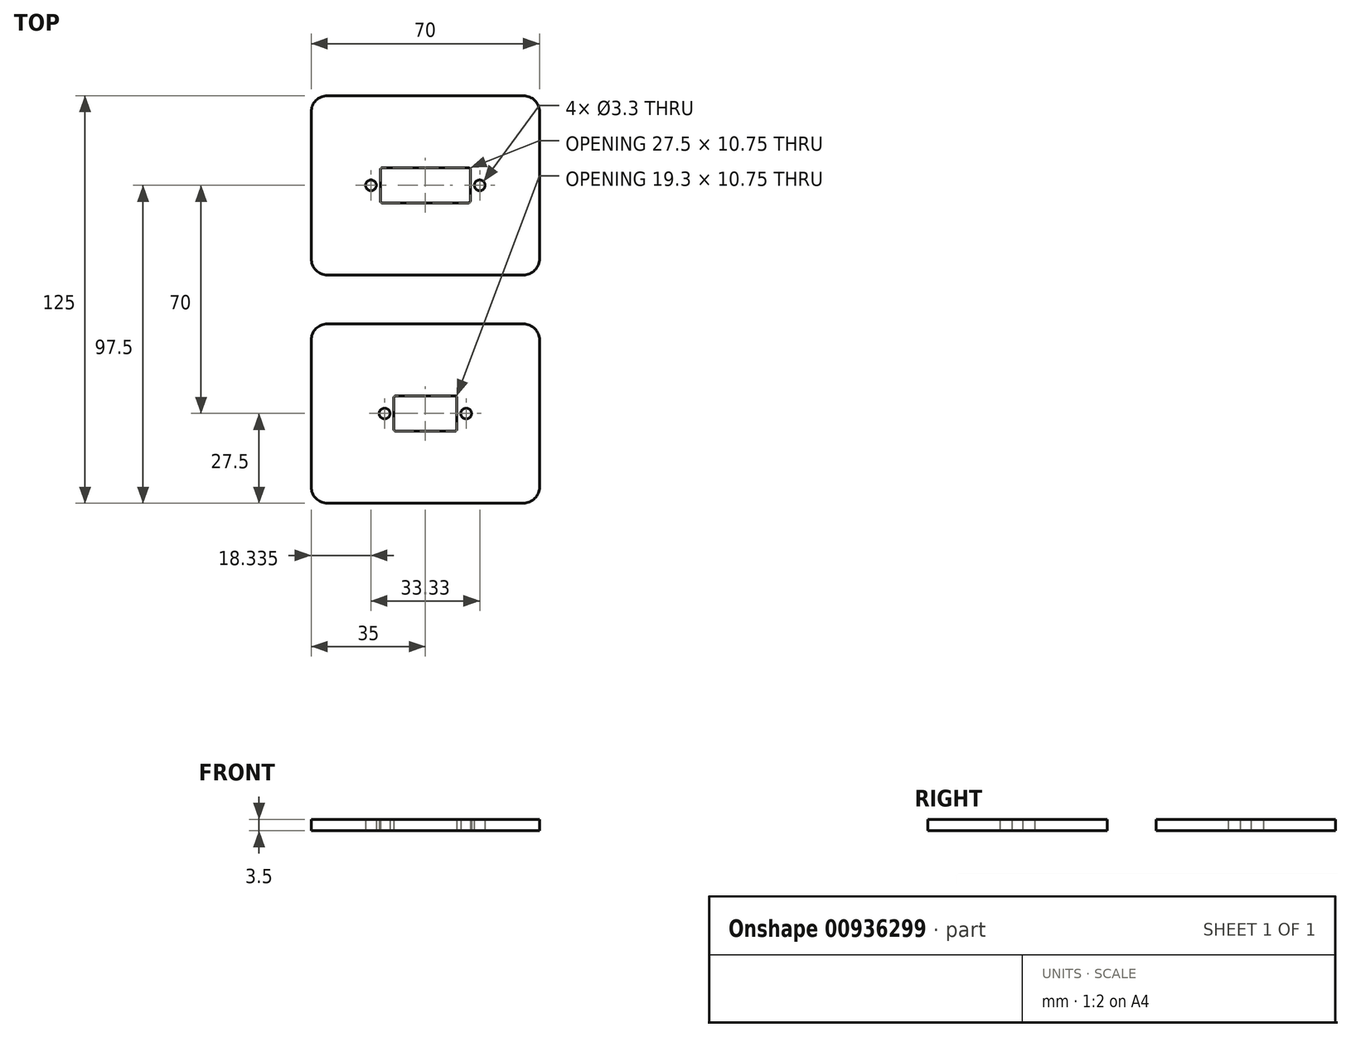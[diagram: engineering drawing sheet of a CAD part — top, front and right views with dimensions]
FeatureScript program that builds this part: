
annotation { "Feature Type Name" : "Feature", "Feature Type Description" : "" }
export const myFeature = defineFeature(function(context is Context, id is Id, definition is map)
    precondition{}
    {
        {
            var Q0;
            Q0=qCreatedBy(makeId("Top.planeOp"),FACE);
            var sketch = newSketch(context, id + "F0", { "sketchPlane" : qUnion([Q0])});
            skPoint(sketch, "E0.middle", {"position": v(0, 0) * mm});
            skLineSegment(sketch, "E1.bottom", {"start": v(35, -27.5) * mm, "end": v(-35, -27.5) * mm});
            skLineSegment(sketch, "E1.top", {"start": v(35, 27.5) * mm, "end": v(-35, 27.5) * mm});
            skLineSegment(sketch, "E1.left", {"start": v(35, -27.5) * mm, "end": v(35, 27.5) * mm});
            skLineSegment(sketch, "E1.right", {"start": v(-35, -27.5) * mm, "end": v(-35, 27.5) * mm});
            skLineSegment(sketch, "E2.bottom", {"start": v(13.75, -5.37) * mm, "end": v(-13.75, -5.38) * mm});
            skLineSegment(sketch, "E2.top", {"start": v(13.75, 5.38) * mm, "end": v(-13.75, 5.37) * mm});
            skLineSegment(sketch, "E2.left", {"start": v(13.75, -5.37) * mm, "end": v(13.75, 5.38) * mm});
            skLineSegment(sketch, "E2.right", {"start": v(-13.75, -5.38) * mm, "end": v(-13.75, 5.37) * mm});
            skCircle(sketch, "E3", {"center": v(0, 0) * mm, "radius": 16.66 * mm, "construction": true});
            skCircle(sketch, "E4", {"center": v(16.66, 0) * mm, "radius": 1.65 * mm});
            skPoint(sketch, "E4.centerSnap0", {"position": v(13.75, 0) * mm});
            skCircle(sketch, "E5", {"center": v(-16.66, 0) * mm, "radius": 1.65 * mm});
            skPoint(sketch, "E6.middle", {"position": v(0, -70) * mm});
            skLineSegment(sketch, "E7.bottom", {"start": v(35, -97.5) * mm, "end": v(-35, -97.5) * mm});
            skLineSegment(sketch, "E7.top", {"start": v(35, -42.5) * mm, "end": v(-35, -42.5) * mm});
            skLineSegment(sketch, "E7.left", {"start": v(35, -97.5) * mm, "end": v(35, -42.5) * mm});
            skLineSegment(sketch, "E7.right", {"start": v(-35, -97.5) * mm, "end": v(-35, -42.5) * mm});
            skLineSegment(sketch, "E8.bottom", {"start": v(9.65, -75.38) * mm, "end": v(-9.65, -75.38) * mm});
            skLineSegment(sketch, "E8.top", {"start": v(9.65, -64.62) * mm, "end": v(-9.65, -64.62) * mm});
            skLineSegment(sketch, "E8.left", {"start": v(9.65, -75.38) * mm, "end": v(9.65, -64.62) * mm});
            skLineSegment(sketch, "E8.right", {"start": v(-9.65, -75.38) * mm, "end": v(-9.65, -64.62) * mm});
            skCircle(sketch, "E9", {"center": v(0, -70) * mm, "radius": 12.5 * mm, "construction": true});
            skCircle(sketch, "E10", {"center": v(12.5, -70) * mm, "radius": 1.65 * mm});
            skPoint(sketch, "E10.centerSnap0", {"position": v(9.65, -70) * mm});
            skCircle(sketch, "E11", {"center": v(-12.5, -70) * mm, "radius": 1.65 * mm});
            skSolve(sketch);
        }
        {
            var Q0;
            Q0=makeQuery(id+"F0.imprint","IMPRINT",FACE,{"disambiguationData":[TD([[makeQuery(id+"F0.imprint","IMPRINT",EDGE,{"derivedFrom":sQuery(id+"F0.wireOp",EDGE,"E1.bottom")}),-1.0]])]});
            var Q1;
            Q1=makeQuery(id+"F0.imprint","IMPRINT",FACE,{"disambiguationData":[TD([[makeQuery(id+"F0.imprint","IMPRINT",EDGE,{"derivedFrom":sQuery(id+"F0.wireOp",EDGE,"E7.bottom")}),-1.0]])]});
            extrude(context, id + "F1", {"entities" : qUnion([Q0, Q1]), "depth" : 3.5 * mm, "offsetDistance" : 25 * mm});
        }
        {
            var Q0;
            Q0=makeQuery(id+"F1.opExtrude","SWEPT_EDGE",EDGE,{"disambiguationData":[OSD([sQuery(id+"F0.wireOp",EDGE,"E1.top"),sQuery(id+"F0.wireOp",EDGE,"E1.left")])]});
            var Q1;
            Q1=makeQuery(id+"F1.opExtrude","SWEPT_EDGE",EDGE,{"disambiguationData":[OSD([sQuery(id+"F0.wireOp",EDGE,"E1.bottom"),sQuery(id+"F0.wireOp",EDGE,"E1.left")])]});
            var Q2;
            Q2=makeQuery(id+"F1.opExtrude","SWEPT_EDGE",EDGE,{"disambiguationData":[OSD([sQuery(id+"F0.wireOp",EDGE,"E7.top"),sQuery(id+"F0.wireOp",EDGE,"E7.left")])]});
            var Q3;
            Q3=makeQuery(id+"F1.opExtrude","SWEPT_EDGE",EDGE,{"disambiguationData":[OSD([sQuery(id+"F0.wireOp",EDGE,"E7.bottom"),sQuery(id+"F0.wireOp",EDGE,"E7.left")])]});
            var Q4;
            Q4=makeQuery(id+"F1.opExtrude","SWEPT_EDGE",EDGE,{"disambiguationData":[OSD([sQuery(id+"F0.wireOp",EDGE,"E7.bottom"),sQuery(id+"F0.wireOp",EDGE,"E7.right")])]});
            var Q5;
            Q5=makeQuery(id+"F1.opExtrude","SWEPT_EDGE",EDGE,{"disambiguationData":[OSD([sQuery(id+"F0.wireOp",EDGE,"E7.top"),sQuery(id+"F0.wireOp",EDGE,"E7.right")])]});
            var Q6;
            Q6=makeQuery(id+"F1.opExtrude","SWEPT_EDGE",EDGE,{"disambiguationData":[OSD([sQuery(id+"F0.wireOp",EDGE,"E1.bottom"),sQuery(id+"F0.wireOp",EDGE,"E1.right")])]});
            var Q7;
            Q7=makeQuery(id+"F1.opExtrude","SWEPT_EDGE",EDGE,{"disambiguationData":[OSD([sQuery(id+"F0.wireOp",EDGE,"E1.top"),sQuery(id+"F0.wireOp",EDGE,"E1.right")])]});
            fillet(context, id + "F2", {"entities" : qUnion([Q0, Q1, Q2, Q3, Q4, Q5, Q6, Q7]), "radius" : 5 * mm, "tangentPropagation" : true, "allowEdgeOverflow" : false});
        }
        {
            var Q0;
            Q0=makeQuery(id+"F1.opExtrude","SWEPT_EDGE",EDGE,{"disambiguationData":[OSD([sQuery(id+"F0.wireOp",EDGE,"E2.bottom"),sQuery(id+"F0.wireOp",EDGE,"E2.left")])]});
            var Q1;
            Q1=makeQuery(id+"F1.opExtrude","SWEPT_EDGE",EDGE,{"disambiguationData":[OSD([sQuery(id+"F0.wireOp",EDGE,"E2.top"),sQuery(id+"F0.wireOp",EDGE,"E2.left")])]});
            var Q2;
            Q2=makeQuery(id+"F1.opExtrude","SWEPT_EDGE",EDGE,{"disambiguationData":[OSD([sQuery(id+"F0.wireOp",EDGE,"E2.top"),sQuery(id+"F0.wireOp",EDGE,"E2.right")])]});
            var Q3;
            Q3=makeQuery(id+"F1.opExtrude","SWEPT_EDGE",EDGE,{"disambiguationData":[OSD([sQuery(id+"F0.wireOp",EDGE,"E2.bottom"),sQuery(id+"F0.wireOp",EDGE,"E2.right")])]});
            var Q4;
            Q4=makeQuery(id+"F1.opExtrude","SWEPT_EDGE",EDGE,{"disambiguationData":[OSD([sQuery(id+"F0.wireOp",EDGE,"E8.top"),sQuery(id+"F0.wireOp",EDGE,"E8.right")])]});
            var Q5;
            Q5=makeQuery(id+"F1.opExtrude","SWEPT_EDGE",EDGE,{"disambiguationData":[OSD([sQuery(id+"F0.wireOp",EDGE,"E8.top"),sQuery(id+"F0.wireOp",EDGE,"E8.left")])]});
            var Q6;
            Q6=makeQuery(id+"F1.opExtrude","SWEPT_EDGE",EDGE,{"disambiguationData":[OSD([sQuery(id+"F0.wireOp",EDGE,"E8.bottom"),sQuery(id+"F0.wireOp",EDGE,"E8.left")])]});
            var Q7;
            Q7=makeQuery(id+"F1.opExtrude","SWEPT_EDGE",EDGE,{"disambiguationData":[OSD([sQuery(id+"F0.wireOp",EDGE,"E8.bottom"),sQuery(id+"F0.wireOp",EDGE,"E8.right")])]});
            fillet(context, id + "F3", {"entities" : qUnion([Q0, Q1, Q2, Q3, Q4, Q5, Q6, Q7]), "radius" : 0.5 * mm, "tangentPropagation" : true, "allowEdgeOverflow" : false});
        }
    });
